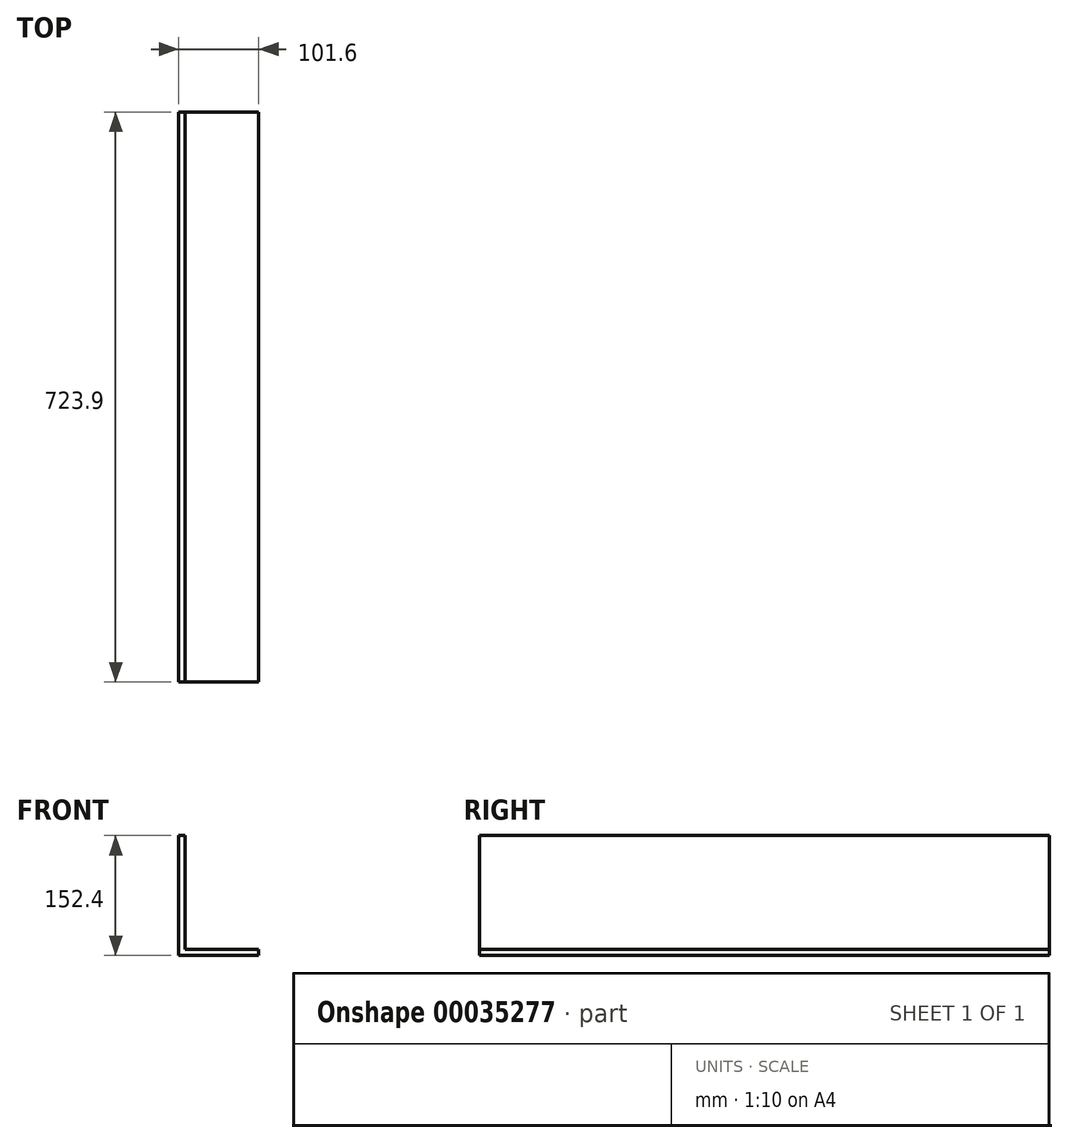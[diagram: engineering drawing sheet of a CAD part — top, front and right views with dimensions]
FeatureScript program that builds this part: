
annotation { "Feature Type Name" : "Feature", "Feature Type Description" : "" }
export const myFeature = defineFeature(function(context is Context, id is Id, definition is map)
    precondition{}
    {
        {
            var Q0;
            Q0=qCreatedBy(makeId("Front.planeOp"),FACE);
            var sketch = newSketch(context, id + "F0", { "sketchPlane" : qUnion([Q0])});
            skLineSegment(sketch, "E0", {"start": v(0, 0) * mm, "end": v(0, 152.4) * mm});
            skLineSegment(sketch, "E1", {"start": v(0, 0) * mm, "end": v(101.6, 0) * mm});
            skLineSegment(sketch, "E2.0", {"start": v(7.94, 7.94) * mm, "end": v(7.94, 152.4) * mm});
            skLineSegment(sketch, "E2.1", {"start": v(7.94, 7.94) * mm, "end": v(101.6, 7.94) * mm});
            skLineSegment(sketch, "E3", {"start": v(101.6, 0) * mm, "end": v(101.6, 7.94) * mm});
            skLineSegment(sketch, "E4", {"start": v(7.94, 152.4) * mm, "end": v(0, 152.4) * mm});
            skSolve(sketch);
        }
        {
            var Q0;
            Q0=qSketchRegion(id+"F0",true);
            extrude(context, id + "F1", {"entities" : qUnion([Q0]), "depth" : 723.9 * mm});
        }
    });
